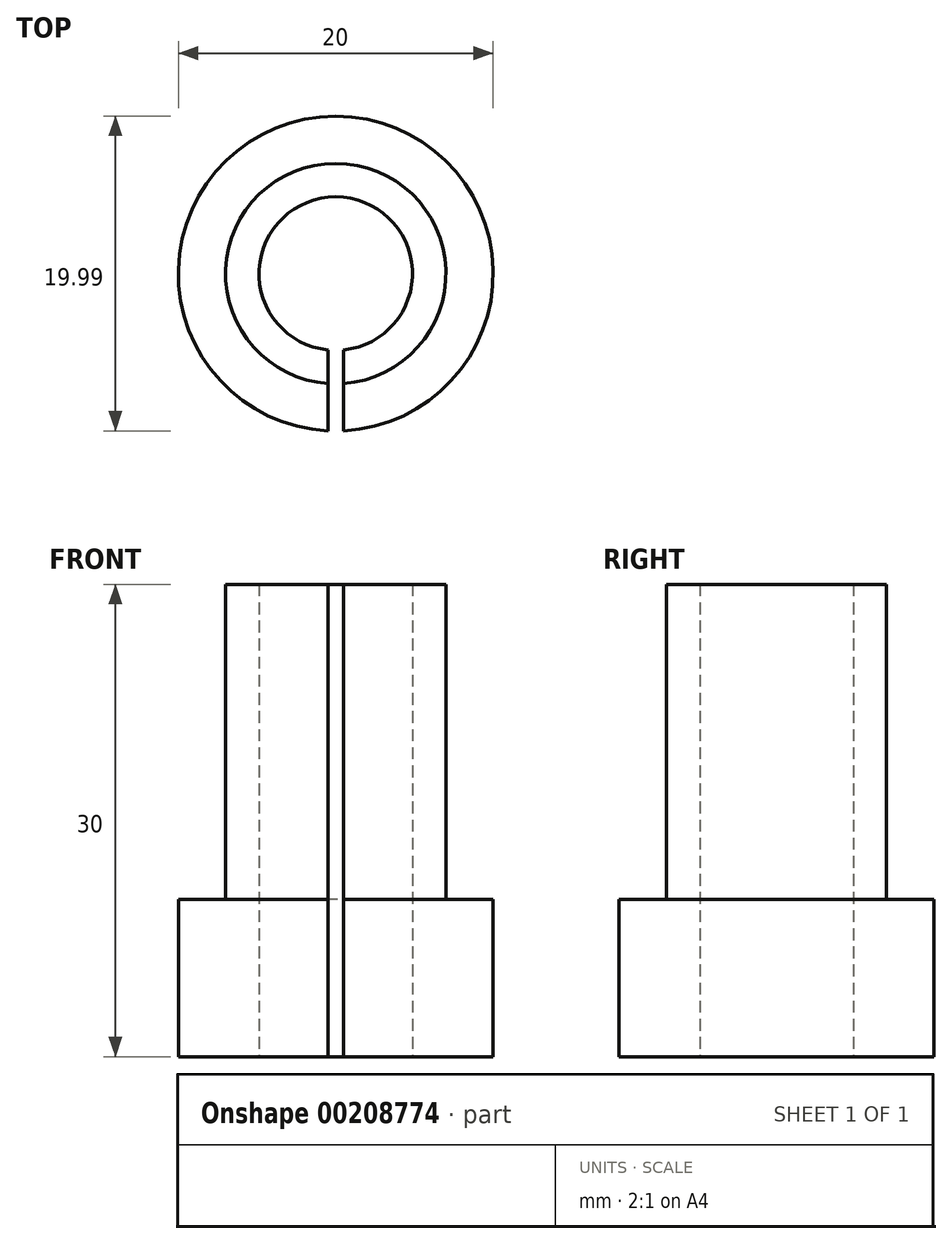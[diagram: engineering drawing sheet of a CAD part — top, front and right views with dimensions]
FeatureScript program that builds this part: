
annotation { "Feature Type Name" : "Feature", "Feature Type Description" : "" }
export const myFeature = defineFeature(function(context is Context, id is Id, definition is map)
    precondition{}
    {
        {
            var Q0;
            Q0=qCreatedBy(makeId("Top.planeOp"),FACE);
            var sketch = newSketch(context, id + "F0", { "sketchPlane" : qUnion([Q0])});
            skCircle(sketch, "E0", {"center": v(0, 0) * mm, "radius": 10 * mm});
            skCircle(sketch, "E1", {"center": v(0, 0) * mm, "radius": 4.88 * mm});
            skLineSegment(sketch, "E2", {"start": v(0, 0) * mm, "end": v(0, -10) * mm, "construction": true});
            skLineSegment(sketch, "E3", {"start": v(0, 0) * mm, "end": v(0.5, 0) * mm, "construction": true});
            skLineSegment(sketch, "E4", {"start": v(0.5, 0) * mm, "end": v(0.5, -9.99) * mm});
            skLineSegment(sketch, "E5.MirrorCS", {"start": v(0, 0) * mm, "end": v(-0.5, 0) * mm, "construction": true});
            skLineSegment(sketch, "E6.MirrorCS", {"start": v(-0.5, 0) * mm, "end": v(-0.5, -9.99) * mm});
            skCircle(sketch, "E7", {"center": v(0, 0) * mm, "radius": 7 * mm});
            skSolve(sketch);
        }
        {
            var Q0;
            {var subQ0=sQuery(id+"F0.wireOp",EDGE,"E4");var subQ1=sQuery(id+"F0.wireOp",EDGE,"E0");var subQ2=makeQuery(id+"F0.imprint","INTERSECT",VERTEX,{"derivedFrom":[subQ1,subQ0]});Q0=makeQuery(id+"F0.imprint","IMPRINT",FACE,{"disambiguationData":[TD([[makeQuery(id+"F0.imprint","IMPRINT",EDGE,{"disambiguationData":[TD([[subQ2,-1.0]])],"derivedFrom":subQ1}),1.0]])]});}
            extrude(context, id + "F1", {"entities" : qUnion([Q0]), "depth" : 10 * mm, "offsetDistance" : 25 * mm});
        }
        {
            var Q0;
            {var subQ0=sQuery(id+"F0.wireOp",EDGE,"E4");var subQ1=sQuery(id+"F0.wireOp",EDGE,"E1");var subQ2=makeQuery(id+"F0.imprint","INTERSECT",VERTEX,{"derivedFrom":[subQ1,subQ0]});Q0=makeQuery(id+"F0.imprint","IMPRINT",FACE,{"disambiguationData":[TD([[makeQuery(id+"F0.imprint","IMPRINT",EDGE,{"disambiguationData":[TD([[subQ2,-1.0]])],"derivedFrom":subQ1}),-1.0]])]});}
            extrude(context, id + "F2", {"entities" : qUnion([Q0]), "operationType" : NewBodyOperationType.ADD, "depth" : 30 * mm, "offsetDistance" : 25 * mm});
        }
    });
